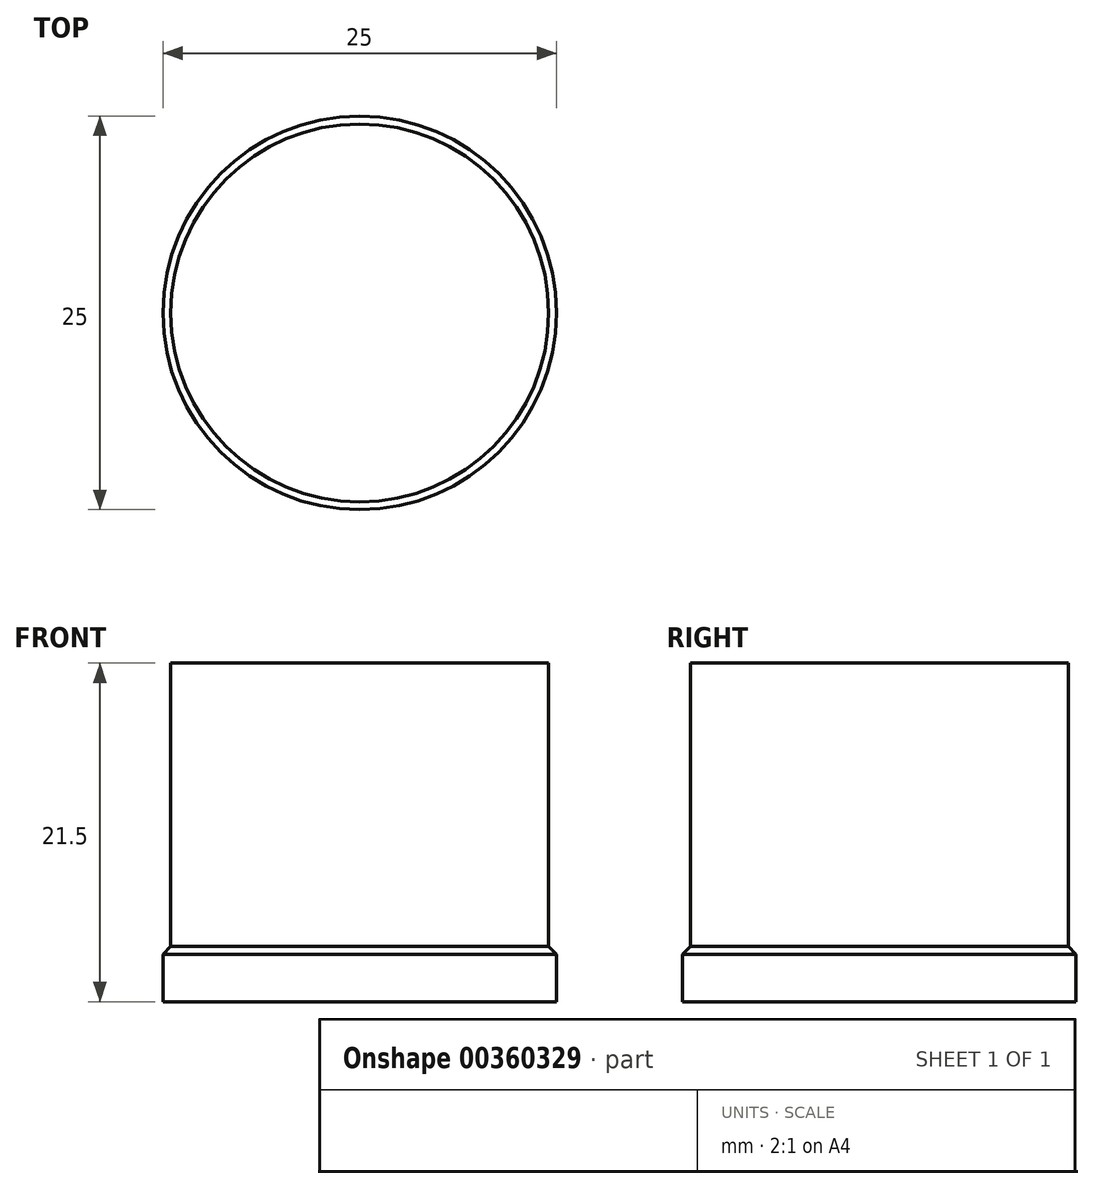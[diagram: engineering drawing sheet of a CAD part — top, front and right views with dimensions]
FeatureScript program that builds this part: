
annotation { "Feature Type Name" : "Feature", "Feature Type Description" : "" }
export const myFeature = defineFeature(function(context is Context, id is Id, definition is map)
    precondition{}
    {
        {
            var Q0;
            Q0=qCreatedBy(makeId("Top.planeOp"),FACE);
            var sketch = newSketch(context, id + "F0", { "sketchPlane" : qUnion([Q0])});
            skCircle(sketch, "E0", {"center": v(0, 0) * mm, "radius": 12.5 * mm});
            skSolve(sketch);
        }
        {
            var Q0;
            Q0=makeQuery(id+"F0.imprint","IMPRINT",FACE,{"disambiguationData":[TD([[makeQuery(id+"F0.imprint","IMPRINT",EDGE,{"derivedFrom":sQuery(id+"F0.wireOp",EDGE,"E0")}),1.0]])]});
            extrude(context, id + "F1", {"entities" : qUnion([Q0]), "depth" : 3 * mm});
        }
        {
            var Q0;
            Q0=makeQuery(id+"F1.opExtrude","CAP_FACE",FACE,{"disambiguationData":[OSD([sQuery(id+"F0.wireOp",EDGE,"E0")])],"isStart":false});
            extrude(context, id + "F2", {"entities" : qUnion([Q0]), "operationType" : NewBodyOperationType.ADD, "depth" : .5 * mm, "hasDraft" : true, "draftAngle" : 45 * degree, "draftPullDirection" : true});
        }
        {
            var Q0;
            Q0=makeQuery(id+"F2.opExtrude","CAP_FACE",FACE,{"disambiguationData":[OSD([sQuery(id+"F0.wireOp",EDGE,"E0")])],"isStart":false});
            extrude(context, id + "F3", {"entities" : qUnion([Q0]), "operationType" : NewBodyOperationType.ADD, "depth" : 18 * mm});
        }
    });
